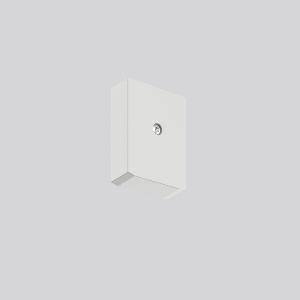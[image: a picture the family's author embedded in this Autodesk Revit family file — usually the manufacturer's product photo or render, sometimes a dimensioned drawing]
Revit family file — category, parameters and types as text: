
# Revit family: linedo_endkappe_b_f_982700_009_3cd6
name_source: partatom
category: Lighting Fixtures
units: mm (PartAtom-declared; Revit-internal decimal feet)

## family parameters
Cut with Voids When Loaded = No
Host = Face
Light Source = No
Part Type = Normal
Room Calculation Point = No
Round Connector Dimension = Use Diameter
Shared = No

## types (1)
- LINEDO_Endkappe_B_F
    Apparent Load = 0 VA
    Default Elevation = 1800 mm
    Description = End cap low profile for LINEDO plug. Plastic end cap to cover the LINEDO plug system at the end of the line. Fastening by TX20 screw. Installation accessories included.
Colour: grey
Length: 23 mm
Width: 58 mm
Height: 76 mm
Weight: 31 g
    Height = 76 mm
    Lamp = 0 x
    Length = 23 mm
    Luminous efficacy = 0 lm/W
    Manufacturer = RZB
    ModVariant = No
    Model = 982700.009
    Mounting Place = Ceiling
    Mounting Type = Surface mounted, Pendant
    Number of Poles = 1
    OnlyDefault = Yes
    Power Factor = 1
    Product Name = LINEDO_Endkappe_B_F
    Product group = Surface mounted continuous line luminaire system
    ProductGroupID = 310
    Protection Class = Protection class
    Protection Degree = Degree of protection
    RLX_Detail_Level = 1
    RLX_Emergency_Light_Flux = 0 lm
    RLX_Emergency_Type = 0
    RLX_Emergency_Type_DB = No
    RlxData = <blob elided: 8509 chars, md5=898a6497>
    Standby Power = 0 W
    System Light Flux = 0 lm
    System Power = 0 W
    Type Comments = Product without accessories
    Type Image = 982700.009.jpg
    URL = http://relux.com
    VarID = ---
    Voltage = 0 V
    Weight = 0.00 kg
    Width = 58 mm

## geometry (parser evidence)
native form markers: Sweep x10
no freeform markers — native parametric forms only
